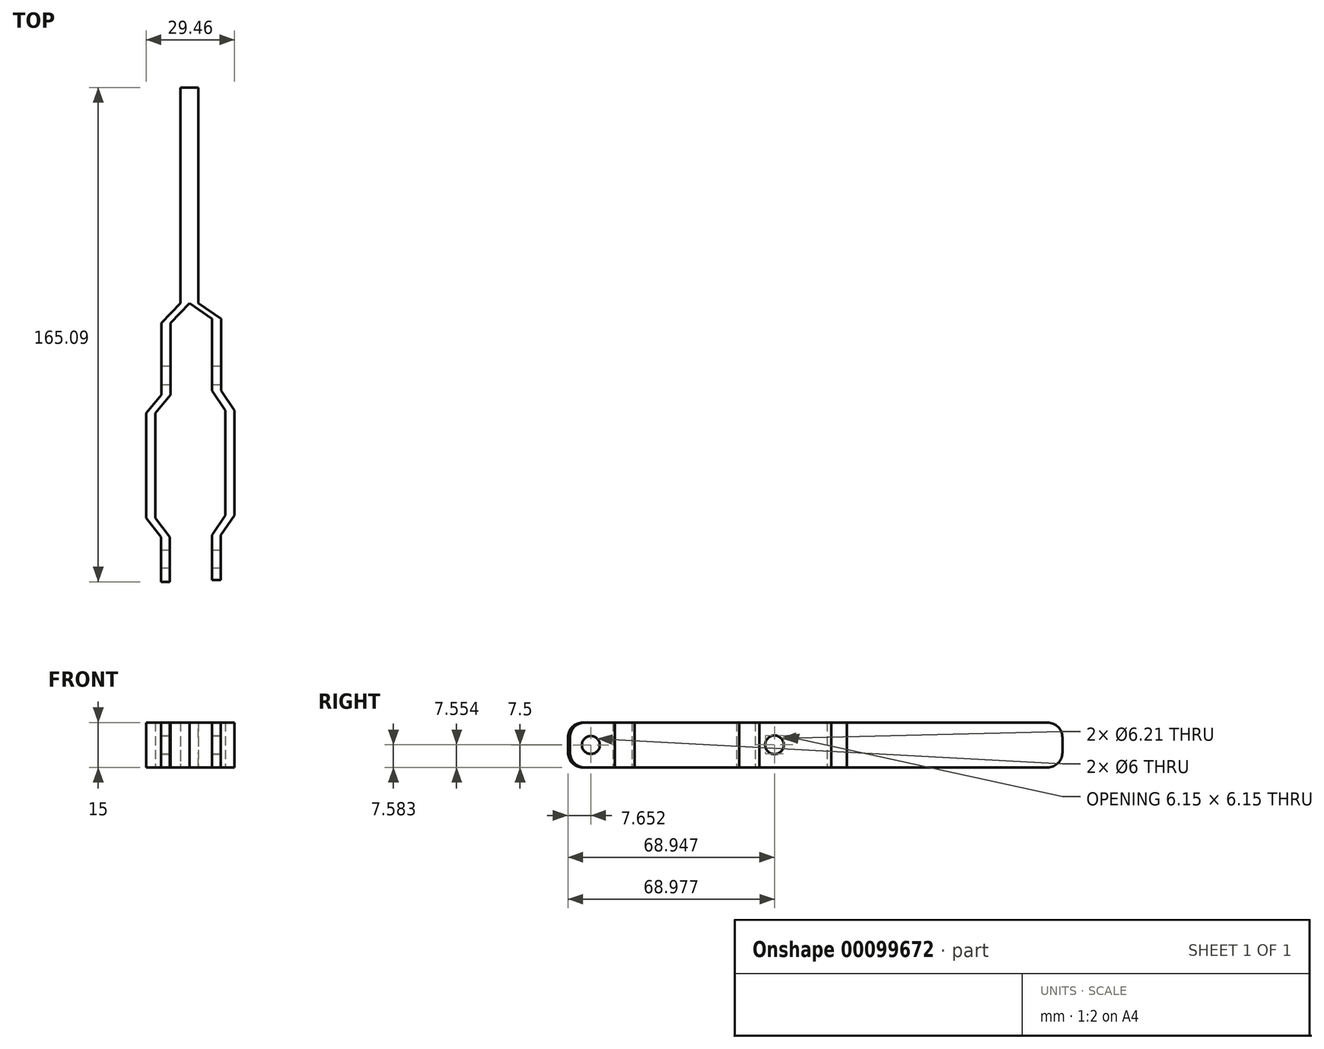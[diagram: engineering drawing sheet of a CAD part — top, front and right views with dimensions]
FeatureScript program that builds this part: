
annotation { "Feature Type Name" : "Feature", "Feature Type Description" : "" }
export const myFeature = defineFeature(function(context is Context, id is Id, definition is map)
    precondition{}
    {
        {
            var Q0;
            Q0=qCreatedBy(makeId("Top.planeOp"),FACE);
            var sketch = newSketch(context, id + "F0", { "sketchPlane" : qUnion([Q0])});
            skLineSegment(sketch, "E0", {"start": v(-3, 72) * mm, "end": v(3, 72) * mm});
            skLineSegment(sketch, "E1", {"start": v(3, 72) * mm, "end": v(3, 0) * mm});
            skLineSegment(sketch, "E2", {"start": v(-3, 0) * mm, "end": v(-3, 72) * mm});
            skLineSegment(sketch, "E3", {"start": v(-3, 0) * mm, "end": v(-9.37, -6.61) * mm});
            skLineSegment(sketch, "E4", {"start": v(-9.37, -6.61) * mm, "end": v(-9.37, -30.61) * mm});
            skLineSegment(sketch, "E5", {"start": v(-9.37, -30.61) * mm, "end": v(-14.46, -36.78) * mm});
            skLineSegment(sketch, "E6", {"start": v(-14.46, -36.78) * mm, "end": v(-14.46, -71.78) * mm});
            skLineSegment(sketch, "E7", {"start": v(-14.46, -71.78) * mm, "end": v(-9.53, -78.09) * mm});
            skLineSegment(sketch, "E8", {"start": v(-9.53, -78.09) * mm, "end": v(-9.53, -93.09) * mm});
            skLineSegment(sketch, "E9", {"start": v(-9.53, -93.09) * mm, "end": v(-6.53, -93.09) * mm});
            skLineSegment(sketch, "E10", {"start": v(-6.53, -93.09) * mm, "end": v(-6.53, -78.09) * mm});
            skLineSegment(sketch, "E11", {"start": v(-6.53, -78.09) * mm, "end": v(-11.46, -71.78) * mm});
            skLineSegment(sketch, "E12", {"start": v(-11.46, -71.78) * mm, "end": v(-11.46, -36.78) * mm});
            skLineSegment(sketch, "E13", {"start": v(-11.46, -36.78) * mm, "end": v(-6.37, -30.61) * mm});
            skLineSegment(sketch, "E14", {"start": v(-6.37, -30.61) * mm, "end": v(-6.37, -6.61) * mm});
            skLineSegment(sketch, "E15", {"start": v(-6.37, -6.61) * mm, "end": v(0, 0) * mm});
            skLineSegment(sketch, "E16", {"start": v(3, 0) * mm, "end": v(10.56, -5.2) * mm});
            skLineSegment(sketch, "E17", {"start": v(10.56, -5.2) * mm, "end": v(10.56, -29.2) * mm});
            skLineSegment(sketch, "E18", {"start": v(10.56, -29.2) * mm, "end": v(15, -35.86) * mm});
            skLineSegment(sketch, "E19", {"start": v(15, -35.86) * mm, "end": v(15, -70.86) * mm});
            skLineSegment(sketch, "E20", {"start": v(15, -70.86) * mm, "end": v(10.47, -77.45) * mm});
            skLineSegment(sketch, "E21", {"start": v(10.47, -77.45) * mm, "end": v(10.47, -92.45) * mm});
            skLineSegment(sketch, "E22", {"start": v(10.47, -92.45) * mm, "end": v(7.47, -92.45) * mm});
            skLineSegment(sketch, "E23", {"start": v(7.47, -92.45) * mm, "end": v(7.47, -77.45) * mm});
            skLineSegment(sketch, "E24", {"start": v(7.47, -77.45) * mm, "end": v(12, -70.86) * mm});
            skLineSegment(sketch, "E25", {"start": v(12, -70.86) * mm, "end": v(12, -35.86) * mm});
            skLineSegment(sketch, "E26", {"start": v(12, -35.86) * mm, "end": v(7.56, -29.2) * mm});
            skLineSegment(sketch, "E27", {"start": v(7.56, -29.2) * mm, "end": v(7.56, -5.2) * mm});
            skLineSegment(sketch, "E28", {"start": v(7.56, -5.2) * mm, "end": v(0, 0) * mm});
            skSolve(sketch);
        }
        {
            var Q0;
            Q0=makeQuery(id+"F0.imprint","IMPRINT",FACE,{"disambiguationData":[TD([[makeQuery(id+"F0.imprint","IMPRINT",EDGE,{"derivedFrom":sQuery(id+"F0.wireOp",EDGE,"E0")}),-1.0]])]});
            extrude(context, id + "F1", {"entities" : qUnion([Q0]), "depth" : 15 * mm});
        }
        {
            var Q0;
            Q0=makeQuery(id+"F1.opExtrude","CAP_EDGE",EDGE,{"disambiguationData":[OSD([sQuery(id+"F0.wireOp",EDGE,"E9")])],"isStart":false});
            var Q1;
            Q1=makeQuery(id+"F1.opExtrude","CAP_EDGE",EDGE,{"disambiguationData":[OSD([sQuery(id+"F0.wireOp",EDGE,"E9")])],"isStart":true});
            var Q2;
            Q2=makeQuery(id+"F1.opExtrude","CAP_EDGE",EDGE,{"disambiguationData":[OSD([sQuery(id+"F0.wireOp",EDGE,"E22")])],"isStart":false});
            var Q3;
            Q3=makeQuery(id+"F1.opExtrude","CAP_EDGE",EDGE,{"disambiguationData":[OSD([sQuery(id+"F0.wireOp",EDGE,"E22")])],"isStart":true});
            fillet(context, id + "F2", {"entities" : qUnion([Q0, Q1, Q2, Q3]), "radius" : 5 * mm, "tangentPropagation" : true, "allowEdgeOverflow" : false});
        }
        {
            var Q0;
            Q0=makeQuery(id+"F1.opExtrude","CAP_EDGE",EDGE,{"disambiguationData":[OSD([sQuery(id+"F0.wireOp",EDGE,"E0")])],"isStart":false});
            var Q1;
            Q1=makeQuery(id+"F1.opExtrude","CAP_EDGE",EDGE,{"disambiguationData":[OSD([sQuery(id+"F0.wireOp",EDGE,"E0")])],"isStart":true});
            fillet(context, id + "F3", {"entities" : qUnion([Q0, Q1]), "radius" : 5 * mm, "tangentPropagation" : true, "allowEdgeOverflow" : false});
        }
        {
            var Q0;
            Q0=makeQuery(id+"F1.opExtrude","SWEPT_FACE",FACE,{"disambiguationData":[OSD([sQuery(id+"F0.wireOp",EDGE,"E17")])]});
            var sketch = newSketch(context, id + "F4", { "sketchPlane" : qUnion([Q0])});
            skCircle(sketch, "E29", {"center": v(-24.14, 7.55) * mm, "radius": 3.1 * mm});
            skSolve(sketch);
        }
        {
            var Q0;
            Q0 = qSketchRegion(id + "F4", true);
            extrude(context, id + "F5", {"entities" : qUnion([Q0]), "operationType" : NewBodyOperationType.REMOVE, "oppositeDirection" : true, "depth" : 25 * mm});
        }
        {
            var Q0;
            Q0=makeQuery(id+"F1.opExtrude","SWEPT_FACE",FACE,{"disambiguationData":[OSD([sQuery(id+"F0.wireOp",EDGE,"E21")])]});
            var sketch = newSketch(context, id + "F6", { "sketchPlane" : qUnion([Q0])});
            skCircle(sketch, "E30", {"center": v(-85.44, 7.5) * mm, "radius": 3 * mm});
            skPoint(sketch, "E30.centerSnap0", {"position": v(-92.45, 7.5) * mm});
            skSolve(sketch);
        }
        {
            var Q0;
            Q0 = qSketchRegion(id + "F6", true);
            extrude(context, id + "F7", {"entities" : qUnion([Q0]), "operationType" : NewBodyOperationType.REMOVE, "oppositeDirection" : true, "depth" : 25 * mm});
        }
    });
